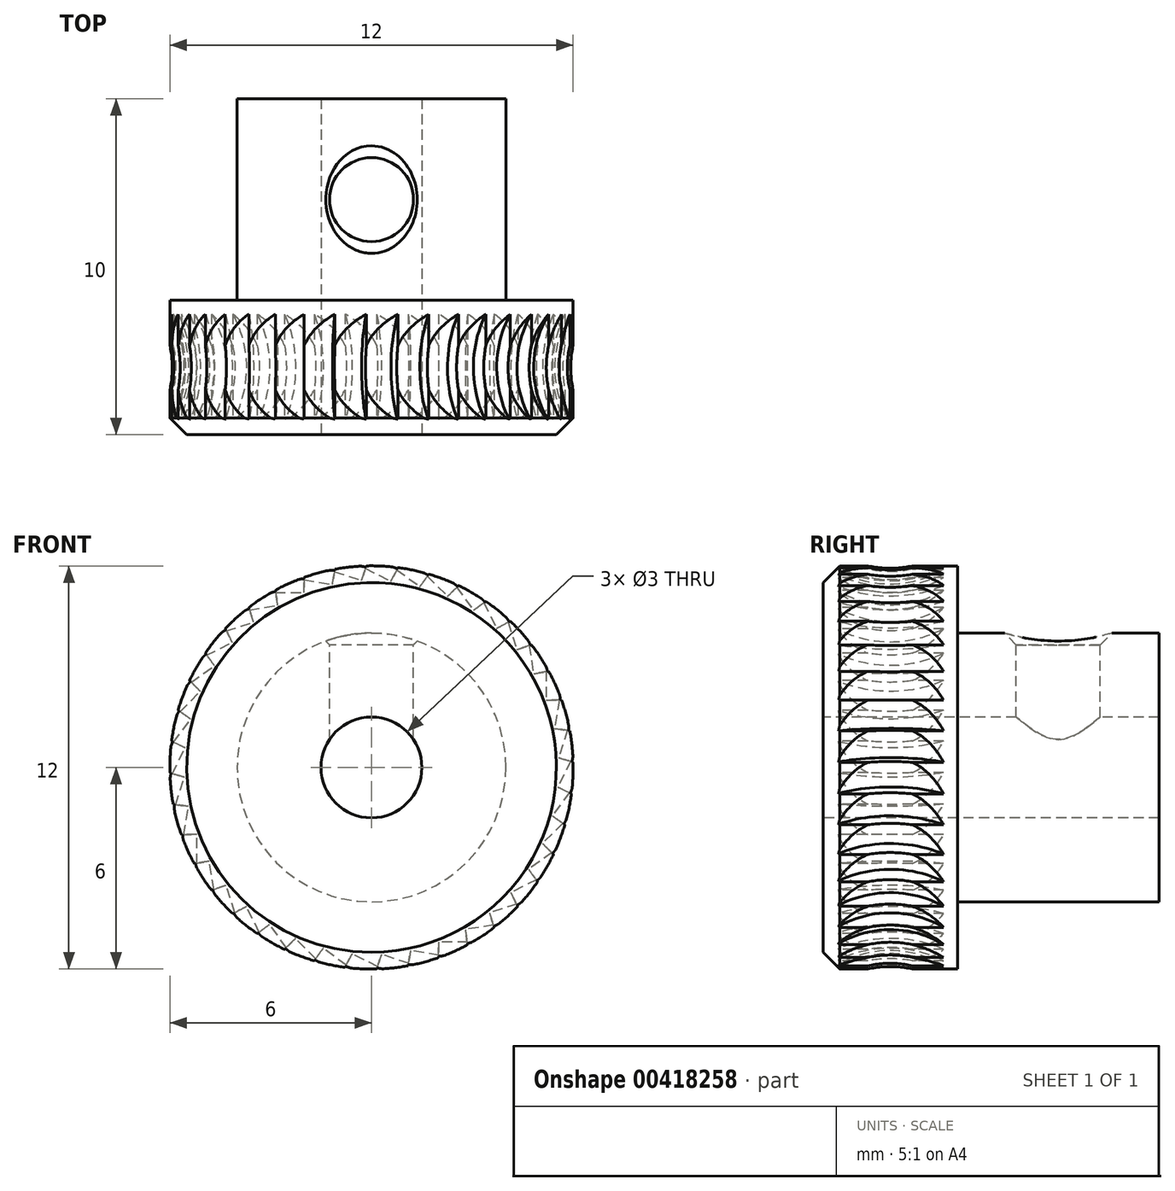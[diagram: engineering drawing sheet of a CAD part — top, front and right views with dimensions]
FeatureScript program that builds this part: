
annotation { "Feature Type Name" : "Feature", "Feature Type Description" : "" }
export const myFeature = defineFeature(function(context is Context, id is Id, definition is map)
    precondition{}
    {
        {
            var Q0;
            Q0=qCreatedBy(makeId("Front.planeOp"),FACE);
            var sketch = newSketch(context, id + "F0", { "sketchPlane" : qUnion([Q0])});
            skCircle(sketch, "E0", {"center": v(0, -2) * mm, "radius": 6 * mm});
            skSolve(sketch);
        }
        {
            var Q0;
            Q0=makeQuery(id+"F0.imprint","IMPRINT",FACE,{"disambiguationData":[TD([[makeQuery(id+"F0.imprint","IMPRINT",EDGE,{"derivedFrom":sQuery(id+"F0.wireOp",EDGE,"E0")}),1.0]])]});
            extrude(context, id + "F1", {"entities" : qUnion([Q0]), "oppositeDirection" : true, "depth" : 10 * mm});
        }
        {
            var Q0;
            Q0=qCreatedBy(makeId("Top.planeOp"),FACE);
            var sketch = newSketch(context, id + "F2", { "sketchPlane" : qUnion([Q0])});
            skCircle(sketch, "E1", {"center": v(8.2, 2) * mm, "radius": 3 * mm});
            skSolve(sketch);
        }
        {
            var Q0;
            Q0 = qSketchRegion(id + "F2", true);
            extrude(context, id + "F3", {"entities" : qUnion([Q0]), "depth" : 10 * mm});
        }
        {
            var Q0;
            Q0=makeQuery(id+"F3.opExtrude","SWEPT_BODY",BODY,{"disambiguationData":[OSD([sQuery(id+"F2.wireOp",EDGE,"E1")])]});
            var Q1;
            Q1=makeQuery(id+"F1.opExtrude","CAP_EDGE",EDGE,{"disambiguationData":[OSD([sQuery(id+"F0.wireOp",EDGE,"E0")])],"isStart":true});
            circularPattern(context, id + "F4", {"operationType" : NewBodyOperationType.REMOVE, "entities" : qUnion([Q0]), "axis" : qUnion([Q1]), "angle" : 360 * degree, "instanceCount" : 40, "equalSpace" : true});
        }
        {
            var Q0;
            Q0=sQuery(id+"F0.wireOp",VERTEX,"E0.center");
            var Q1;
            Q1=makeQuery(id+"F1.opExtrude","SWEPT_BODY",BODY,{"disambiguationData":[OSD([sQuery(id+"F0.wireOp",EDGE,"E0")])]});
            hole(context, id + "F5", {"style" : HoleStyle.SIMPLE, "endStyle" : HoleEndStyle.THROUGH, "holeDiameter" : 3 * mm, "isTappedThrough" : true, "tappedDepth" : 12 * mm, "tapClearance" : 3, "locations" : qUnion([Q0]), "scope" : qUnion([Q1])});
        }
        {
            var Q0;
            Q0=makeQuery(id+"F1.opExtrude","CAP_FACE",FACE,{"disambiguationData":[OSD([sQuery(id+"F0.wireOp",EDGE,"E0")])],"isStart":false});
            var sketch = newSketch(context, id + "F6", { "sketchPlane" : qUnion([Q0])});
            skCircle(sketch, "E2", {"center": v(0, -2) * mm, "radius": 4 * mm});
            skSolve(sketch);
        }
        {
            var Q0;
            Q0=makeQuery(id+"F6.imprint","IMPRINT",FACE,{"disambiguationData":[TD([[makeQuery(id+"F6.imprint","IMPRINT",EDGE,{"derivedFrom":sQuery(id+"F6.wireOp",EDGE,"E2")}),-1.0]])]});
            extrude(context, id + "F7", {"entities" : qUnion([Q0]), "operationType" : NewBodyOperationType.REMOVE, "oppositeDirection" : true, "depth" : 6 * mm});
        }
        {
            var Q0;
            Q0=makeQuery(id+"F1.opExtrude","CAP_EDGE",EDGE,{"disambiguationData":[OSD([sQuery(id+"F0.wireOp",EDGE,"E0")])],"isStart":true});
            var Q1;
            Q1=makeQuery(id+"F5.hole-0.boolean.opBoolean","COPY",EDGE,{"derivedFrom":makeQuery(id+"F5.hole-0.opRevolve","SWEPT_EDGE",EDGE,{"disambiguationData":[OSD([sQuery(id+"F5.hole-0.sketch.wireOp",EDGE,"core_line_2"),sQuery(id+"F5.hole-0.sketch.wireOp",EDGE,"core_line_3")])]})});
            var Q2;
            Q2=makeQuery(id+"F5.hole-0.boolean.opBoolean","INTERSECT",EDGE,{"derivedFrom":[makeQuery(id+"F1.opExtrude","CAP_FACE",FACE,{"disambiguationData":[OSD([sQuery(id+"F0.wireOp",EDGE,"E0")])],"isStart":false}),makeQuery(id+"F5.hole-0.opRevolve","SWEPT_FACE",FACE,{"disambiguationData":[OSD([sQuery(id+"F5.hole-0.sketch.wireOp",EDGE,"core_line_2")])]})]});
            var Q3;
            Q3=makeQuery(id+"F1.opExtrude","CAP_EDGE",EDGE,{"disambiguationData":[OSD([sQuery(id+"F0.wireOp",EDGE,"E0")])],"isStart":false});
            var Q4;
            Q4=makeQuery(id+"F7.boolean.opBoolean","COPY",EDGE,{"derivedFrom":makeQuery(id+"F7.opExtrude","CAP_EDGE",EDGE,{"disambiguationData":[OSD([sQuery(id+"F0.wireOp",EDGE,"E0")])],"isStart":false})});
            var Q5;
            Q5=makeQuery(id+"F7.boolean.opBoolean","COPY",EDGE,{"derivedFrom":makeQuery(id+"F7.opExtrude","CAP_EDGE",EDGE,{"disambiguationData":[OSD([sQuery(id+"F6.wireOp",EDGE,"E2")])],"isStart":true})});
            chamfer(context, id + "F8", {"entities" : qUnion([Q0, Q1, Q2, Q3, Q4, Q5]), "width" : 0.5 * mm, "tangentPropagation" : true});
        }
        {
            var Q0;
            Q0=qCreatedBy(makeId("Top.planeOp"),FACE);
            cPlane(context, id + "F9", {"entities" : qUnion([Q0]), "cplaneType" : CPlaneType.OFFSET, "offset" : 2 * mm, "width" : 150 * mm, "height" : 150 * mm});
        }
        {
            var Q0;
            Q0=qCreatedBy(id+"F9.planeOp",FACE);
            var sketch = newSketch(context, id + "F10", { "sketchPlane" : qUnion([Q0])});
            skPoint(sketch, "E3", {"position": v(0, 7) * mm});
            skSolve(sketch);
        }
        {
            var Q0;
            Q0=sQuery(id+"F10.wireOp",VERTEX,"E3");
            var Q1;
            Q1=makeQuery(id+"F1.opExtrude","SWEPT_BODY",BODY,{"disambiguationData":[OSD([sQuery(id+"F0.wireOp",EDGE,"E0")])]});
            hole(context, id + "F11", {"style" : HoleStyle.C_SINK, "endStyle" : HoleEndStyle.BLIND, "holeDiameter" : 2.5 * mm, "cSinkDiameter" : 3.2 * mm, "cSinkAngle" : 90 * degree, "holeDepth" : 4 * mm, "isTappedThrough" : true, "tappedDepth" : 12 * mm, "tapClearance" : 3, "startFromSketch" : true, "locations" : qUnion([Q0]), "scope" : qUnion([Q1])});
        }
    });
